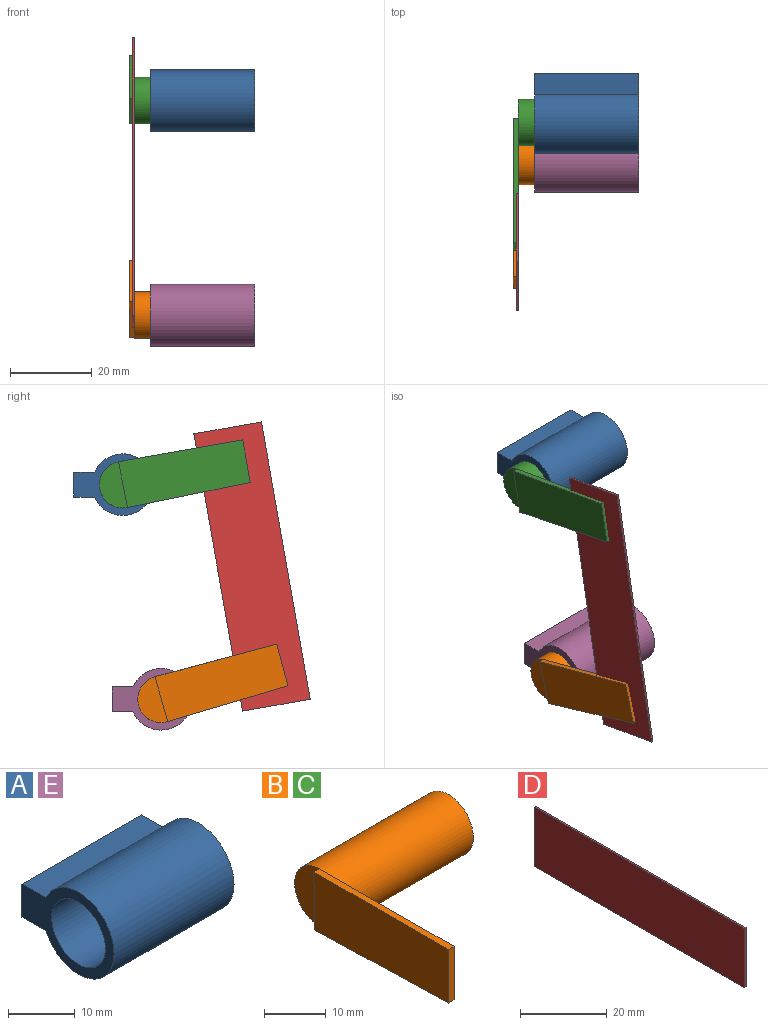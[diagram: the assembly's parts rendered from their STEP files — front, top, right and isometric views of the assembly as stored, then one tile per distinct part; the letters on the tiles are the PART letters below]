
ASSEMBLY  parts=5 mates=4
PART A: 7 faces, bbox 25.4x19.5x15 mm
  f0: plane 25.4x6.06mm, normal (0,1,0), area 154mm2, adj f1,f3,f5,f6
  f1: plane 25.4x5.09mm, normal (0,0,1), area 129.2mm2, adj f0,f2,f5,f6
  f2: cylinder r=7.52mm len=25.4mm, axis (-1,0,0), area 1041.9mm2, adj f1,f3,f5,f6
  f3: plane 25.4x5.09mm, normal (0,0,-1), area 129.2mm2, adj f0,f2,f5,f6
  f4: cylinder r=5.69mm len=25.4mm, axis (-1,0,0), area 908.7mm2, adj f5,f6
  f5: plane 19.49x15.04mm, normal (1,0,0), area 104.1mm2, adj f0,f1,f2,f3,f4
  f6: plane 19.49x15.04mm, normal (-1,0,0), area 104.1mm2, adj f0,f1,f2,f3,f4
PART B: 9 faces, bbox 30.7x36.4x11.4 mm
  f0: plane 11.39x5.85mm, normal (-1,0,0), area 51.6mm2, adj f1,f4
  f1: cylinder r=5.69mm len=29.46mm, axis (-1,0,0), area 1054mm2, adj f0,f2,f3,f8
  f2: plane 11.39x11.39mm, normal (1,0,0), area 101.8mm2, adj f1
  f3: plane 30.78x1.27mm, normal (0,0,1), area 39.1mm2, adj f1,f4,f6,f7,f8
  f4: plane 11.39x1.27mm, normal (0,1,-0.02), area 14.5mm2, adj f0,f3,f5,f7
  f5: plane 30.59x1.27mm, normal (0,-0.03,-1), area 38.9mm2, adj f4,f6,f7,f8
  f6: plane 10.56x1.27mm, normal (0,-1,0), area 13.4mm2, adj f3,f5,f7,f8
  f7: plane 30.78x11.39mm, normal (-1,0,0), area 336.6mm2, adj f3,f4,f5,f6
  f8: plane 30.7x11.39mm, normal (1,0,0), area 286.4mm2, adj f1,f3,f5,f6
PART C: same geometry as B
PART D: 6 faces, bbox 0.5x68.7x16.8 mm
  f0: plane 16.75x0.51mm, normal (0,1,0), area 8.5mm2, adj f1,f3,f4,f5
  f1: plane 68.72x0.51mm, normal (0,0,1), area 34.9mm2, adj f0,f2,f4,f5
  f2: plane 16.75x0.51mm, normal (0,-1,0), area 8.5mm2, adj f1,f3,f4,f5
  f3: plane 68.72x0.51mm, normal (0,0,-1), area 34.9mm2, adj f0,f2,f4,f5
  f4: plane 68.72x16.75mm, normal (1,0,0), area 1151.2mm2, adj f0,f1,f2,f3
  f5: plane 68.72x16.75mm, normal (-1,0,0), area 1151.2mm2, adj f0,f1,f2,f3
PART E: same geometry as A
PLACE A t=(18.5,-38.01,18.05)mm
PLACE B rot(axis=(-1,0,0),15deg) t=(16.47,-46,-24.15)mm
PLACE C rot(axis=(-1,0,0),10deg) t=(16.47,-37.39,24.88)mm
PLACE D rot(axis=(1,0,0),80deg) t=(1.23,12.59,-1.03)mm
PLACE E t=(18.5,-47.37,-34.32)mm
MATE revolute B.f8 <-> D.f4  axis (1,0,0) through (1.74,-34.63,-27.06)mm
MATE revolute C.f8 <-> D.f4  axis (1,0,0) through (1.74,-25.81,22.97)mm
MATE revolute C.f1 <-> A.f2  axis (1,0,0) through (31.2,1.34,17.94)mm
MATE revolute B.f1 <-> E.f2  axis (1,0,0) through (31.2,-8.03,-34.44)mm
